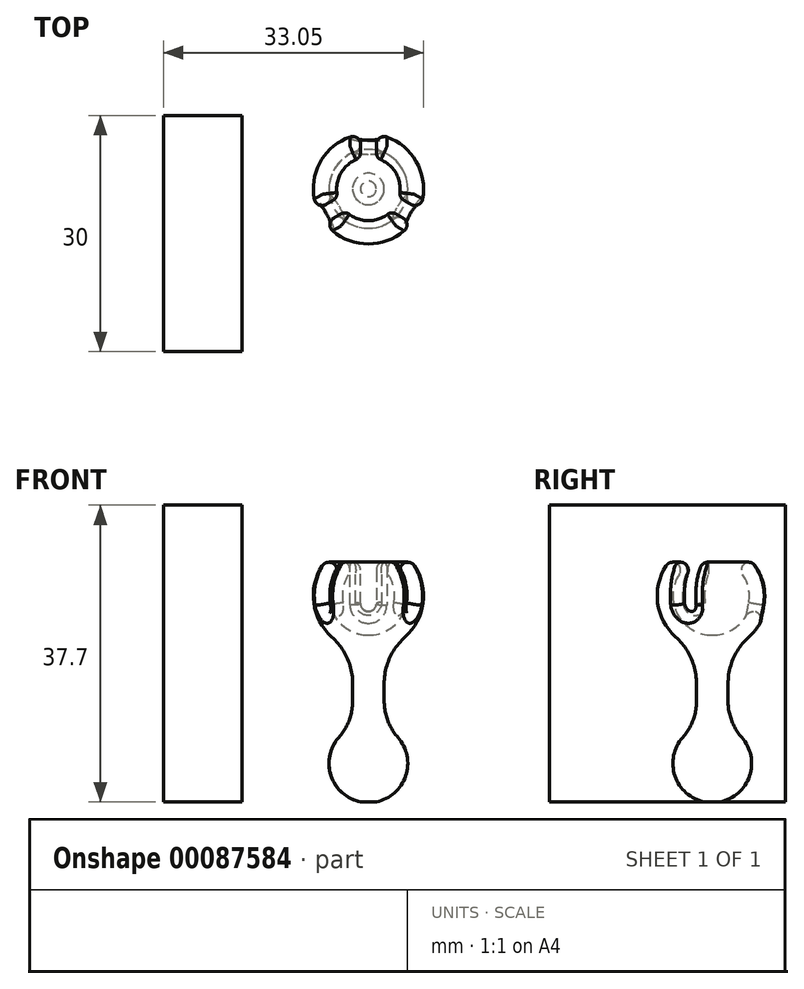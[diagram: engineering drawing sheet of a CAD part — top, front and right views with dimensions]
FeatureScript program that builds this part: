
annotation { "Feature Type Name" : "Feature", "Feature Type Description" : "" }
export const myFeature = defineFeature(function(context is Context, id is Id, definition is map)
    precondition{}
    {
        {
            var Q0;
            Q0=qCreatedBy(makeId("Front.planeOp"),FACE);
            var sketch = newSketch(context, id + "F0", { "sketchPlane" : qUnion([Q0])});
            skArc(sketch, "E0", {"start": v(-4.2, 2.72) * mm, "mid": v(-4.4, -2.39) * mm, "end": v(0, -5) * mm});
            skArc(sketch, "E1", {"start": v(-5.87, 3.81) * mm, "mid": v(-6.57, -2.42) * mm, "end": v(-2, -6.7) * mm});
            skLineSegment(sketch, "E2", {"start": v(-4.2, 2.72) * mm, "end": v(-5.87, 3.81) * mm, "construction": true});
            skLineSegment(sketch, "E3", {"start": v(0, -5) * mm, "end": v(0, -13.57) * mm, "construction": true});
            skArc(sketch, "E4", {"start": v(-4.2, 2.72) * mm, "mid": v(-4.49, 4.1) * mm, "end": v(-5.87, 3.81) * mm});
            skPoint(sketch, "E5.endSnap0", {"position": v(0, -6.78) * mm});
            skLineSegment(sketch, "E6.trimOffspring", {"start": v(0, -5) * mm, "end": v(0, -7) * mm});
            skLineSegment(sketch, "E7", {"start": v(-2, -6.7) * mm, "end": v(-2, -16.7) * mm});
            skLineSegment(sketch, "E8", {"start": v(0, -15) * mm, "end": v(0, -7) * mm});
            skArc(sketch, "E9", {"start": v(-2, -16.7) * mm, "mid": v(-4.97, -21.82) * mm, "end": v(-1, -26.19) * mm});
            skLineSegment(sketch, "E10", {"start": v(0, -15) * mm, "end": v(0, -26.3) * mm});
            skLineSegment(sketch, "E11", {"start": v(-1, -26.19) * mm, "end": v(0, -26.19) * mm});
            skCircle(sketch, "E12", {"center": v(0, 6.54) * mm, "radius": 5 * mm, "construction": true});
            skLineSegment(sketch, "E13", {"start": v(-5, 11.6) * mm, "end": v(-5, -24.85) * mm, "construction": true});
            skCircle(sketch, "E14", {"center": v(0, 0) * mm, "radius": 5 * mm, "construction": true});
            skLineSegment(sketch, "E15", {"start": v(-4.2, 2.72) * mm, "end": v(-4.2, -8.13) * mm, "construction": true});
            skSolve(sketch);
        }
        {
            var Q0;
            Q0=makeQuery(id+"F0.imprint","IMPRINT",FACE,{"disambiguationData":[TD([[makeQuery(id+"F0.imprint","IMPRINT",EDGE,{"derivedFrom":sQuery(id+"F0.wireOp",EDGE,"E0")}),-1.0]])]});
            var Q1;
            Q1=sQuery(id+"F0.wireOp",EDGE,"E8");
            revolve(context, id + "F1", {"entities" : qUnion([Q0]), "axis" : qUnion([Q1]), "revolveType" : RevolveType.FULL});
        }
        {
            var Q0;
            Q0=qCreatedBy(makeId("Top.planeOp"),FACE);
            cPlane(context, id + "F2", {"entities" : qUnion([Q0]), "cplaneType" : CPlaneType.OFFSET, "offset" : 5 * mm, "width" : 150 * mm, "height" : 150 * mm});
        }
        {
            var Q0;
            Q0=qCreatedBy(id+"F2.planeOp",FACE);
            var sketch = newSketch(context, id + "F3", { "sketchPlane" : qUnion([Q0])});
            skLineSegment(sketch, "E16", {"start": v(0, 0) * mm, "end": v(0, 9.47) * mm, "construction": true});
            skLineSegment(sketch, "E17.bottom", {"start": v(1, 9.47) * mm, "end": v(-1, 9.47) * mm});
            skLineSegment(sketch, "E17.top", {"start": v(1, 0) * mm, "end": v(-1, 0) * mm});
            skLineSegment(sketch, "E17.left", {"start": v(1, 9.47) * mm, "end": v(1, 0) * mm});
            skLineSegment(sketch, "E17.right", {"start": v(-1, 9.47) * mm, "end": v(-1, 0) * mm});
            skPoint(sketch, "E17.middle", {"position": v(0, 4.73) * mm});
            skPoint(sketch, "E18.1.0", {"position": v(-4.1, -2.37) * mm});
            skLineSegment(sketch, "E18.1.1", {"start": v(-7.7, -5.6) * mm, "end": v(0.5, -0.87) * mm});
            skLineSegment(sketch, "E18.1.2", {"start": v(-8.7, -3.87) * mm, "end": v(-0.5, 0.87) * mm});
            skLineSegment(sketch, "E18.1.3", {"start": v(-0.5, 0.87) * mm, "end": v(0.5, -0.87) * mm});
            skLineSegment(sketch, "E18.1.4", {"start": v(0, 0) * mm, "end": v(-8.2, -4.73) * mm, "construction": true});
            skLineSegment(sketch, "E18.1.5", {"start": v(-8.7, -3.87) * mm, "end": v(-7.7, -5.6) * mm});
            skPoint(sketch, "E18.2.0", {"position": v(4.1, -2.37) * mm});
            skLineSegment(sketch, "E18.2.1", {"start": v(8.7, -3.87) * mm, "end": v(0.5, 0.87) * mm});
            skLineSegment(sketch, "E18.2.2", {"start": v(7.7, -5.6) * mm, "end": v(-0.5, -0.87) * mm});
            skLineSegment(sketch, "E18.2.3", {"start": v(-0.5, -0.87) * mm, "end": v(0.5, 0.87) * mm});
            skLineSegment(sketch, "E18.2.4", {"start": v(0, 0) * mm, "end": v(8.2, -4.73) * mm, "construction": true});
            skLineSegment(sketch, "E18.2.5", {"start": v(7.7, -5.6) * mm, "end": v(8.7, -3.87) * mm});
            skPoint(sketch, "E18.center", {"position": v(0, 0) * mm});
            skSolve(sketch);
        }
        {
            var Q0;
            Q0 = qSketchRegion(id + "F3", true);
            extrude(context, id + "F4", {"entities" : qUnion([Q0]), "operationType" : NewBodyOperationType.REMOVE, "oppositeDirection" : true, "depth" : 7 * mm});
        }
        {
            var Q0;
            Q0=makeQuery(id+"F4.boolean.opBoolean","COPY",EDGE,{"derivedFrom":makeQuery(id+"F4.opExtrude","CAP_EDGE",EDGE,{"disambiguationData":[OSD([sQuery(id+"F3.wireOp",EDGE,"E18.1.2")])],"isStart":false})});
            var Q1;
            Q1=makeQuery(id+"F4.boolean.opBoolean","COPY",EDGE,{"derivedFrom":makeQuery(id+"F4.opExtrude","CAP_EDGE",EDGE,{"disambiguationData":[OSD([sQuery(id+"F3.wireOp",EDGE,"E18.1.1")])],"isStart":false})});
            var Q2;
            Q2=makeQuery(id+"F4.boolean.opBoolean","COPY",EDGE,{"derivedFrom":makeQuery(id+"F4.opExtrude","CAP_EDGE",EDGE,{"disambiguationData":[OSD([sQuery(id+"F3.wireOp",EDGE,"E18.2.1")])],"isStart":false})});
            var Q3;
            Q3=makeQuery(id+"F4.boolean.opBoolean","COPY",EDGE,{"derivedFrom":makeQuery(id+"F4.opExtrude","CAP_EDGE",EDGE,{"disambiguationData":[OSD([sQuery(id+"F3.wireOp",EDGE,"E18.2.2")])],"isStart":false})});
            var Q4;
            Q4=makeQuery(id+"F4.boolean.opBoolean","COPY",EDGE,{"derivedFrom":makeQuery(id+"F4.opExtrude","CAP_EDGE",EDGE,{"disambiguationData":[OSD([sQuery(id+"F3.wireOp",EDGE,"E17.right")])],"isStart":false})});
            var Q5;
            Q5=makeQuery(id+"F4.boolean.opBoolean","COPY",EDGE,{"derivedFrom":makeQuery(id+"F4.opExtrude","CAP_EDGE",EDGE,{"disambiguationData":[OSD([sQuery(id+"F3.wireOp",EDGE,"E17.left")])],"isStart":false})});
            fillet(context, id + "F5", {"entities" : qUnion([Q0, Q1, Q2, Q3, Q4, Q5]), "radius" : 1 * mm, "tangentPropagation" : true, "allowEdgeOverflow" : false});
        }
        {
            var Q0;
            Q0=makeQuery(id+"F4.boolean.opBoolean","INTERSECT",EDGE,{"derivedFrom":[makeQuery(id+"F1.opRevolve","SWEPT_FACE",FACE,{"disambiguationData":[OSD([sQuery(id+"F0.wireOp",EDGE,"E1")])]}),makeQuery(id+"F4.opExtrude","SWEPT_FACE",FACE,{"disambiguationData":[OSD([sQuery(id+"F3.wireOp",EDGE,"E18.2.1")])]})]});
            var Q1;
            Q1=makeQuery(id+"F4.boolean.opBoolean","INTERSECT",EDGE,{"derivedFrom":[makeQuery(id+"F1.opRevolve","SWEPT_FACE",FACE,{"disambiguationData":[OSD([sQuery(id+"F0.wireOp",EDGE,"E1")])]}),makeQuery(id+"F4.opExtrude","SWEPT_FACE",FACE,{"disambiguationData":[OSD([sQuery(id+"F3.wireOp",EDGE,"E17.right")])]})]});
            var Q2;
            Q2=makeQuery(id+"F4.boolean.opBoolean","INTERSECT",EDGE,{"derivedFrom":[makeQuery(id+"F1.opRevolve","SWEPT_FACE",FACE,{"disambiguationData":[OSD([sQuery(id+"F0.wireOp",EDGE,"E1")])]}),makeQuery(id+"F4.opExtrude","SWEPT_FACE",FACE,{"disambiguationData":[OSD([sQuery(id+"F3.wireOp",EDGE,"E18.1.2")])]})]});
            fillet(context, id + "F6", {"entities" : qUnion([Q0, Q1, Q2]), "radius" : 1 * mm, "tangentPropagation" : true, "allowEdgeOverflow" : false});
        }
        {
            var Q0;
            Q0=makeQuery(id+"F1.opRevolve","SWEPT_EDGE",EDGE,{"disambiguationData":[OSD([sQuery(id+"F0.wireOp",EDGE,"E1"),sQuery(id+"F0.wireOp",EDGE,"E7")])]});
            fillet(context, id + "F7", {"entities" : qUnion([Q0]), "radius" : 8 * mm, "tangentPropagation" : true, "allowEdgeOverflow" : false});
        }
        {
            var Q0;
            Q0=makeQuery(id+"F1.opRevolve","SWEPT_EDGE",EDGE,{"disambiguationData":[OSD([sQuery(id+"F0.wireOp",EDGE,"E7"),sQuery(id+"F0.wireOp",EDGE,"ywg5SL3T-TYOw-sGt6-3Rzi-PARAZnVLxAsf")])]});
            fillet(context, id + "F8", {"entities" : qUnion([Q0]), "radius" : 7 * mm, "tangentPropagation" : true, "allowEdgeOverflow" : false});
        }
        {
            var Q0;
            Q0=makeQuery(id+"F1.opRevolve","SWEPT_FACE",FACE,{"disambiguationData":[OSD([sQuery(id+"F0.wireOp",EDGE,"E11")])]});
            var sketch = newSketch(context, id + "F9", { "sketchPlane" : qUnion([Q0])});
            skLineSegment(sketch, "E19.bottom", {"start": v(-26.05, -9.32) * mm, "end": v(-16.05, -9.32) * mm});
            skLineSegment(sketch, "E19.top", {"start": v(-26.05, 20.68) * mm, "end": v(-16.05, 20.68) * mm});
            skLineSegment(sketch, "E19.left", {"start": v(-26.05, -9.32) * mm, "end": v(-26.05, 20.68) * mm});
            skLineSegment(sketch, "E19.right", {"start": v(-16.05, -9.32) * mm, "end": v(-16.05, 20.68) * mm});
            skSolve(sketch);
        }
        {
            var Q0;
            Q0=makeQuery(id+"F9.imprint","IMPRINT",FACE,{"disambiguationData":[TD([[makeQuery(id+"F9.imprint","IMPRINT",EDGE,{"derivedFrom":sQuery(id+"F9.wireOp",EDGE,"E19.bottom")}),1.0]])]});
            extrude(context, id + "F10", {"entities" : qUnion([Q0]), "oppositeDirection" : true, "depth" : 37.7 * mm});
        }
    });
